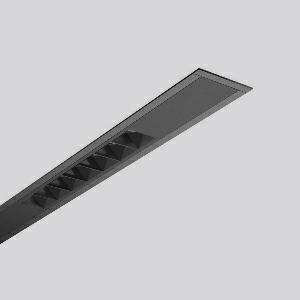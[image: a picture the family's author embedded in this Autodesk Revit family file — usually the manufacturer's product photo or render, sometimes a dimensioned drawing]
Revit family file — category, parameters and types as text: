
# Revit family: less_is_more_beamline_312467_003_1_65eb
name_source: partatom
category: Lighting Fixtures
units: mm (PartAtom-declared; Revit-internal decimal feet)

## family parameters
Cut with Voids When Loaded = No
Host = Face
Light Source = No
Part Type = Normal
Room Calculation Point = No
Round Connector Dimension = Use Diameter
Shared = No

## types (1)
- LESS IS MORE BEAMLINE (1 x LED Modul 940, 1100 lm, 4000)
    Apparent Load = 23 VA
    CIE Flux Codes = 100 100 100 100 100
    Color Rendering = 92
    Color Temperature = 4000
    Default Elevation = 1800 mm
    Description = Series: LESS IS MORE BEAMLINE
Linear recessed ceiling and wall luminaire for aesthetically sophisticated lighting. Luminaire with two LED light units. Housing: extruded aluminium profile, powder-coated. End cap aluminium powder-coated. LED light unit with MRS technology: Mini-Reflector-System made of metallised thermoplastic with prismatic black glare-suppressing frame for pleasant glare-free light (RUG < 10). Each LED light unit has 7 reflector elements. Wide beam light distribution. Ceiling installation with pre-assembled SBS mounting system. LED unit with integrated converter interchangeable and removable. Suitable for through-wiring. 
Colour: deep black, matt (RAL 9005)
Length: 1141 mm
Width: 71 mm
Height: 1.5 mm
Cut-out length: 1128 mm
Cut-out width: 60 mm
Recess height: 125 mm
Luminaire: recess height: 106 mm
Lamp: LED
Socket: without socket
Colour temperature: 4000K
Colour rendering index (CRI): 90
System power: 23 W
Rated luminous flux: 2200 lm
Luminous efficiency: 96 lm/W
Control gear: Regulated power supply
Protection class: I
Type of protection: IP 20
    Height = 0 mm  [stored 0 ft]
    Lamp = 1 x LED Modul 940
    Lamp Light Flux = 1100 lm
    Lamp count = 1
    Length = 1141 mm
    Lifetime = 50000 h
    Luminous efficacy = 96 lm/W
    Manufacturer = RZB
    ModVariant = No
    Model = 312467.003.1
    Mounting Place = Ceiling, Wall
    Mounting Type = Recessed
    Number of Poles = 1
    OnlyDefault = Yes
    Power Factor = 1
    Product Name = LESS IS MORE BEAMLINE
    Product group = Recessed LED linear luminaires
    ProductGroupID = 407
    Protection Class = Protection class I
    Protection Degree = IP 20
    RLX_Detail_Level = 1
    RLX_Emergency_Light_Flux = 0 lm
    RLX_Emergency_Type = 0
    RLX_Emergency_Type_DB = No
    RlxData = <blob elided: 23869 chars, md5=e784781d>
    Socket = socket
    Standby Power = 0 W
    System Light Flux = 2200 lm
    System Power = 23 W
    Type Comments = Product without accessories
    Type Image = 312465.003.jpg
    URL = http://relux.com
    VarID = ---
    Voltage = 230 V
    Voltage Range = 220-240 V
    Weight = 0.00 kg
    Width = 71 mm

note: [stored X ft] marks values corroborated as IEEE doubles in the binary element streams (Revit-internal decimal feet)

## geometry (parser evidence)
native form markers: Blend x4, Sweep x14
no freeform markers — native parametric forms only
